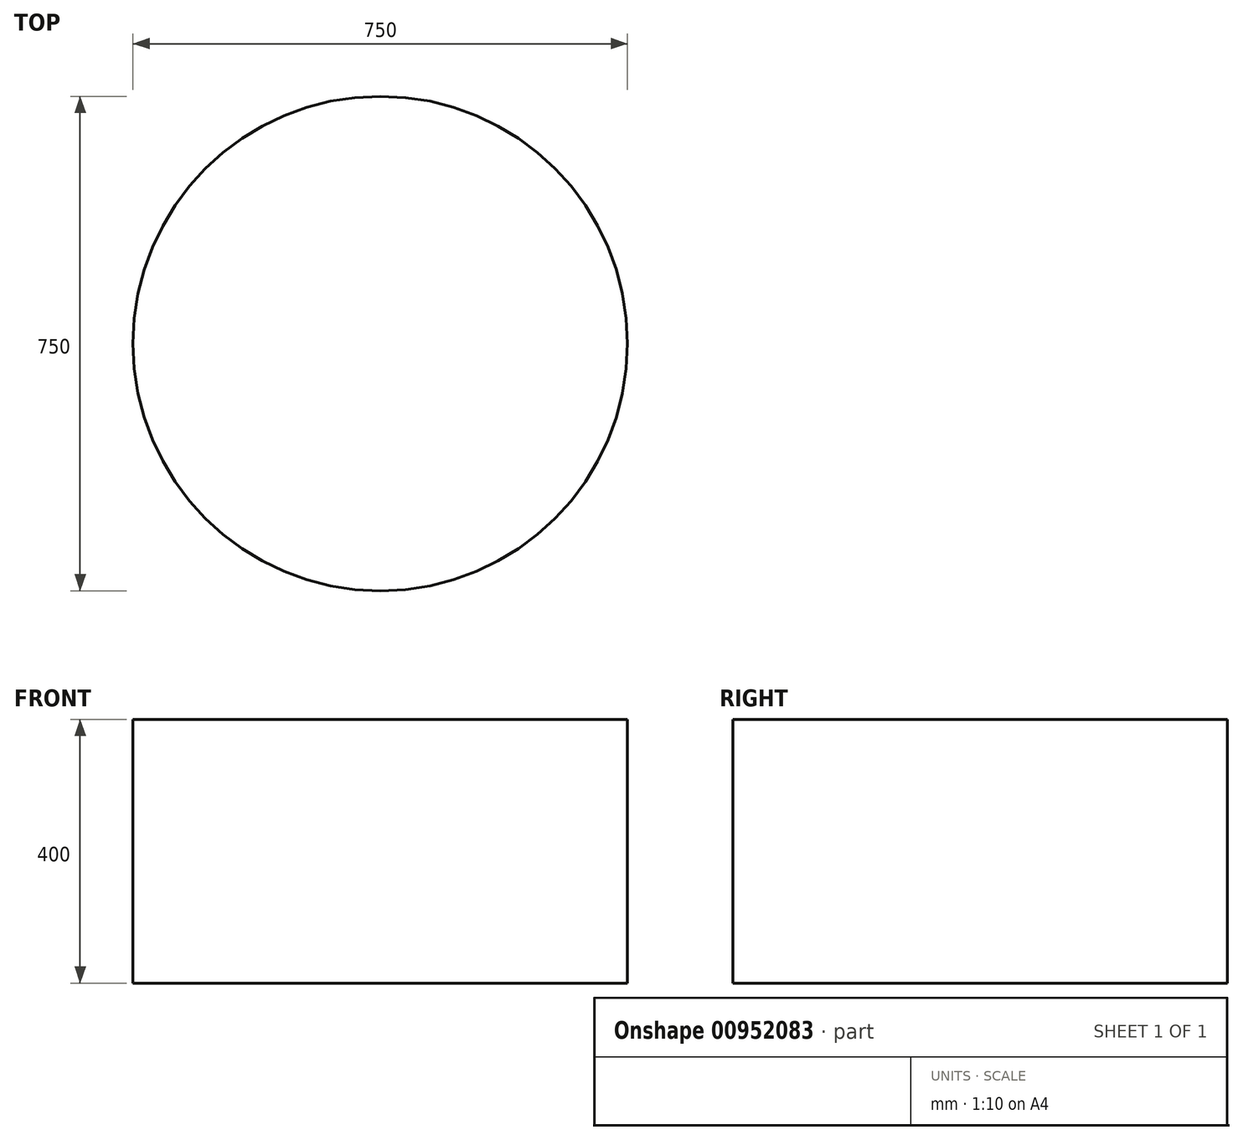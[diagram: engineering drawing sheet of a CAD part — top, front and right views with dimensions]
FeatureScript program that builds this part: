
annotation { "Feature Type Name" : "Feature", "Feature Type Description" : "" }
export const myFeature = defineFeature(function(context is Context, id is Id, definition is map)
    precondition{}
    {
        {
            var Q0;
            Q0=qCreatedBy(makeId("Top.planeOp"),FACE);
            var sketch = newSketch(context, id + "F0", { "sketchPlane" : qUnion([Q0])});
            skCircle(sketch, "E0", {"center": v(0, 0) * mm, "radius": 375 * mm});
            skSolve(sketch);
        }
        {
            var Q0;
            Q0 = qSketchRegion(id + "F0", true);
            extrude(context, id + "F1", {"entities" : qUnion([Q0]), "depth" : 400 * mm, "offsetDistance" : 25 * mm});
        }
        {
            var Q0;
            Q0=qCreatedBy(makeId("Front.planeOp"),FACE);
            cPlane(context, id + "F2", {"entities" : qUnion([Q0]), "cplaneType" : CPlaneType.OFFSET, "offset" : 375 * mm, "oppositeDirection" : true, "width" : 150 * mm, "height" : 150 * mm});
        }
    });
